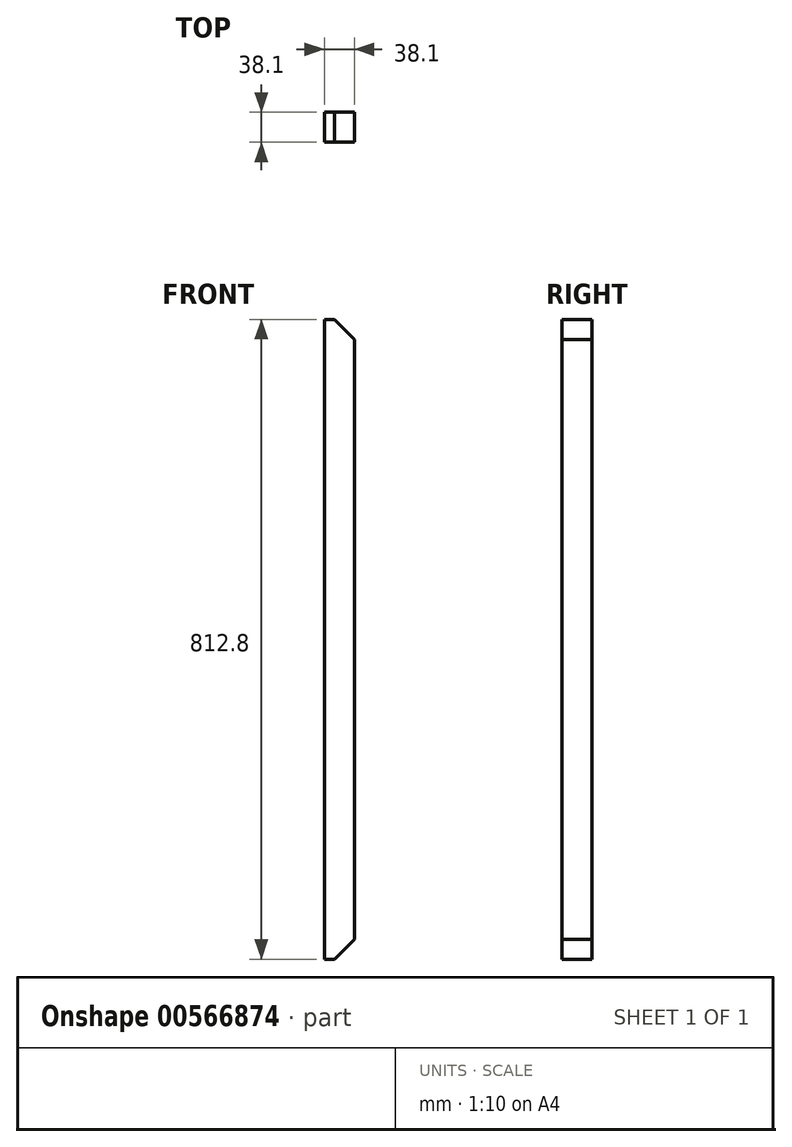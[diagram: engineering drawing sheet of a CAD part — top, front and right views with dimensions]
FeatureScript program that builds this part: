
annotation { "Feature Type Name" : "Feature", "Feature Type Description" : "" }
export const myFeature = defineFeature(function(context is Context, id is Id, definition is map)
    precondition{}
    {
        {
            var Q0;
            Q0=qCreatedBy(makeId("Front.planeOp"),FACE);
            var sketch = newSketch(context, id + "F0", { "sketchPlane" : qUnion([Q0])});
            skLineSegment(sketch, "E0.bottom", {"start": v(19.05, -406.4) * mm, "end": v(-19.05, -406.4) * mm});
            skLineSegment(sketch, "E0.top", {"start": v(19.05, 406.4) * mm, "end": v(-19.05, 406.4) * mm});
            skLineSegment(sketch, "E0.left", {"start": v(19.05, -406.4) * mm, "end": v(19.05, 406.4) * mm});
            skLineSegment(sketch, "E0.right", {"start": v(-19.05, -406.4) * mm, "end": v(-19.05, 406.4) * mm});
            skPoint(sketch, "E0.middle", {"position": v(0, 0) * mm});
            skSolve(sketch);
        }
        {
            var Q0;
            Q0 = qSketchRegion(id + "F0", true);
            extrude(context, id + "F1", {"entities" : qUnion([Q0]), "depth" : 38.1 * mm, "offsetDistance" : 25.4 * mm});
        }
        {
            var Q0;
            Q0=makeQuery(id+"F1.opExtrude","CAP_FACE",FACE,{"disambiguationData":[OSD([sQuery(id+"F0.wireOp",EDGE,"E0.bottom"),sQuery(id+"F0.wireOp",EDGE,"E0.top"),sQuery(id+"F0.wireOp",EDGE,"E0.left"),sQuery(id+"F0.wireOp",EDGE,"E0.right")])],"isStart":false});
            var sketch = newSketch(context, id + "F2", { "sketchPlane" : qUnion([Q0])});
            skLineSegment(sketch, "E1", {"start": v(-6.35, 406.4) * mm, "end": v(19.05, 381) * mm});
            skLineSegment(sketch, "E2", {"start": v(-6.35, 406.4) * mm, "end": v(19.05, 406.4) * mm});
            skLineSegment(sketch, "E3", {"start": v(19.05, 406.4) * mm, "end": v(19.05, 381) * mm});
            skLineSegment(sketch, "E4", {"start": v(-6.35, -406.4) * mm, "end": v(19.05, -381) * mm});
            skLineSegment(sketch, "E5", {"start": v(19.05, -381) * mm, "end": v(19.05, -406.4) * mm});
            skLineSegment(sketch, "E6", {"start": v(19.05, -406.4) * mm, "end": v(-6.35, -406.4) * mm});
            skSolve(sketch);
        }
        {
            var Q0;
            Q0=makeQuery(id+"F2.imprint","IMPRINT",FACE,{"disambiguationData":[TD([[makeQuery(id+"F2.imprint","IMPRINT",EDGE,{"derivedFrom":sQuery(id+"F2.wireOp",EDGE,"E4")}),-1.0]])]});
            var Q1;
            Q1=makeQuery(id+"F2.imprint","IMPRINT",FACE,{"disambiguationData":[TD([[makeQuery(id+"F2.imprint","IMPRINT",EDGE,{"derivedFrom":sQuery(id+"F2.wireOp",EDGE,"E1")}),1.0]])]});
            extrude(context, id + "F3", {"entities" : qUnion([Q0, Q1]), "operationType" : NewBodyOperationType.REMOVE, "endBound" : BoundingType.THROUGH_ALL, "oppositeDirection" : true, "depth" : 25.4 * mm, "offsetDistance" : 25.4 * mm});
        }
    });
